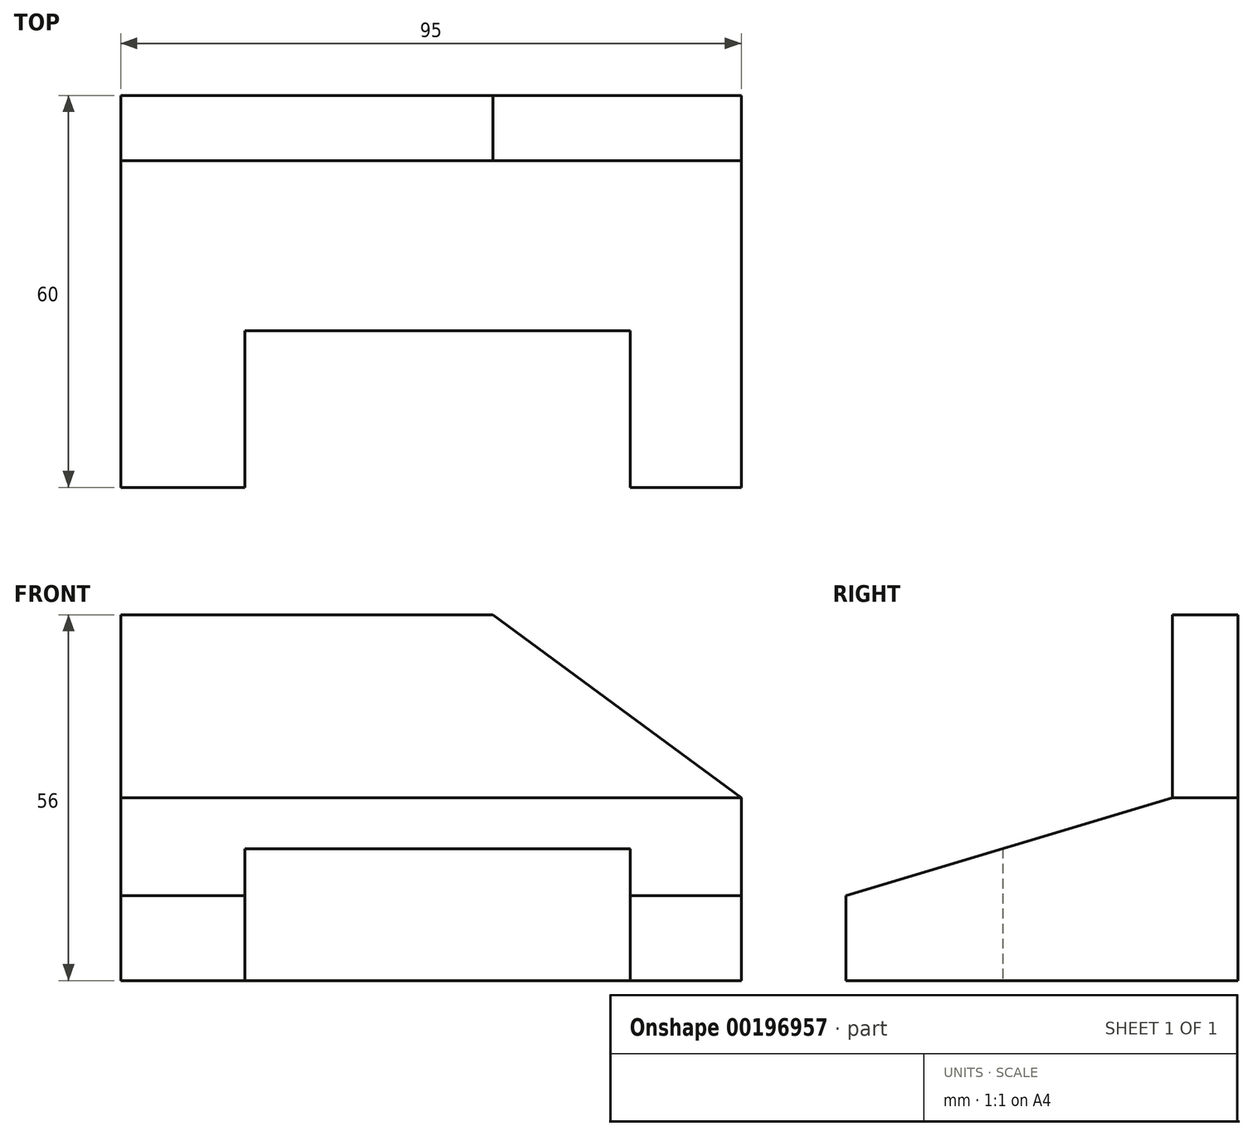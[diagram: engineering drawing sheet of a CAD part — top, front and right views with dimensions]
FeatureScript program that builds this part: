
annotation { "Feature Type Name" : "Feature", "Feature Type Description" : "" }
export const myFeature = defineFeature(function(context is Context, id is Id, definition is map)
    precondition{}
    {
        {
            var Q0;
            Q0=qCreatedBy(makeId("Right.planeOp"),FACE);
            var sketch = newSketch(context, id + "F0", { "sketchPlane" : qUnion([Q0])});
            skLineSegment(sketch, "E0.bottom", {"start": v(-30, 0) * mm, "end": v(30, 0) * mm});
            skLineSegment(sketch, "E0.top", {"start": v(-30, 56) * mm, "end": v(30, 56) * mm});
            skLineSegment(sketch, "E0.left", {"start": v(-30, 0) * mm, "end": v(-30, 56) * mm});
            skLineSegment(sketch, "E0.right", {"start": v(30, 0) * mm, "end": v(30, 56) * mm});
            skLineSegment(sketch, "E1", {"start": v(-30, 13) * mm, "end": v(20, 28) * mm});
            skLineSegment(sketch, "E2", {"start": v(20, 28) * mm, "end": v(20, 56) * mm});
            skSolve(sketch);
        }
        {
            var Q0;
            {var subQ2=sQuery(id+"F0.wireOp",EDGE,"E0.bottom");Q0=makeQuery(id+"F0.imprint","IMPRINT",FACE,{"disambiguationData":[TD([[makeQuery(id+"F0.imprint","IMPRINT",EDGE,{"derivedFrom":subQ2}),1.0]])]});}
            extrude(context, id + "F1", {"entities" : qUnion([Q0]), "endBound" : BoundingType.SYMMETRIC, "depth" : 95 * mm});
        }
        {
            var Q0;
            Q0=qCreatedBy(makeId("Top.planeOp"),FACE);
            var sketch = newSketch(context, id + "F2", { "sketchPlane" : qUnion([Q0])});
            skLineSegment(sketch, "E3.bottom", {"start": v(-28.5, -30) * mm, "end": v(30.5, -30) * mm});
            skLineSegment(sketch, "E3.top", {"start": v(-28.5, -6) * mm, "end": v(30.5, -6) * mm});
            skLineSegment(sketch, "E3.left", {"start": v(-28.5, -30) * mm, "end": v(-28.5, -6) * mm});
            skLineSegment(sketch, "E3.right", {"start": v(30.5, -30) * mm, "end": v(30.5, -6) * mm});
            skSolve(sketch);
        }
        {
            var Q0;
            Q0=makeQuery(id+"F2.imprint","IMPRINT",FACE,{"disambiguationData":[TD([[makeQuery(id+"F2.imprint","IMPRINT",EDGE,{"derivedFrom":sQuery(id+"F2.wireOp",EDGE,"E3.bottom")}),1.0]])]});
            extrude(context, id + "F3", {"entities" : qUnion([Q0]), "operationType" : NewBodyOperationType.REMOVE, "depth" : 25 * mm});
        }
        {
            var Q0;
            Q0=makeQuery(id+"F1.opExtrude","SWEPT_FACE",FACE,{"disambiguationData":[OSD([sQuery(id+"F0.wireOp",EDGE,"E2")])]});
            var sketch = newSketch(context, id + "F4", { "sketchPlane" : qUnion([Q0])});
            skLineSegment(sketch, "E4", {"start": v(9.5, 56) * mm, "end": v(47.5, 28) * mm});
            skSolve(sketch);
        }
        {
            var Q0;
            Q0=makeQuery(id+"F4.imprint","IMPRINT",FACE,{"disambiguationData":[TD([[makeQuery(id+"F4.imprint","IMPRINT",EDGE,{"derivedFrom":sQuery(id+"F4.wireOp",EDGE,"E4")}),1.0]])]});
            var Q1;
            Q1=makeQuery(id+"F1.opExtrude","SWEPT_FACE",FACE,{"disambiguationData":[OSD([sQuery(id+"F0.wireOp",EDGE,"E0.right")])]});
            extrude(context, id + "F5", {"entities" : qUnion([Q0]), "operationType" : NewBodyOperationType.REMOVE, "endBound" : BoundingType.UP_TO_SURFACE, "oppositeDirection" : true, "endBoundEntityFace" : qUnion([Q1]), "depth" : 30 * mm});
        }
    });
